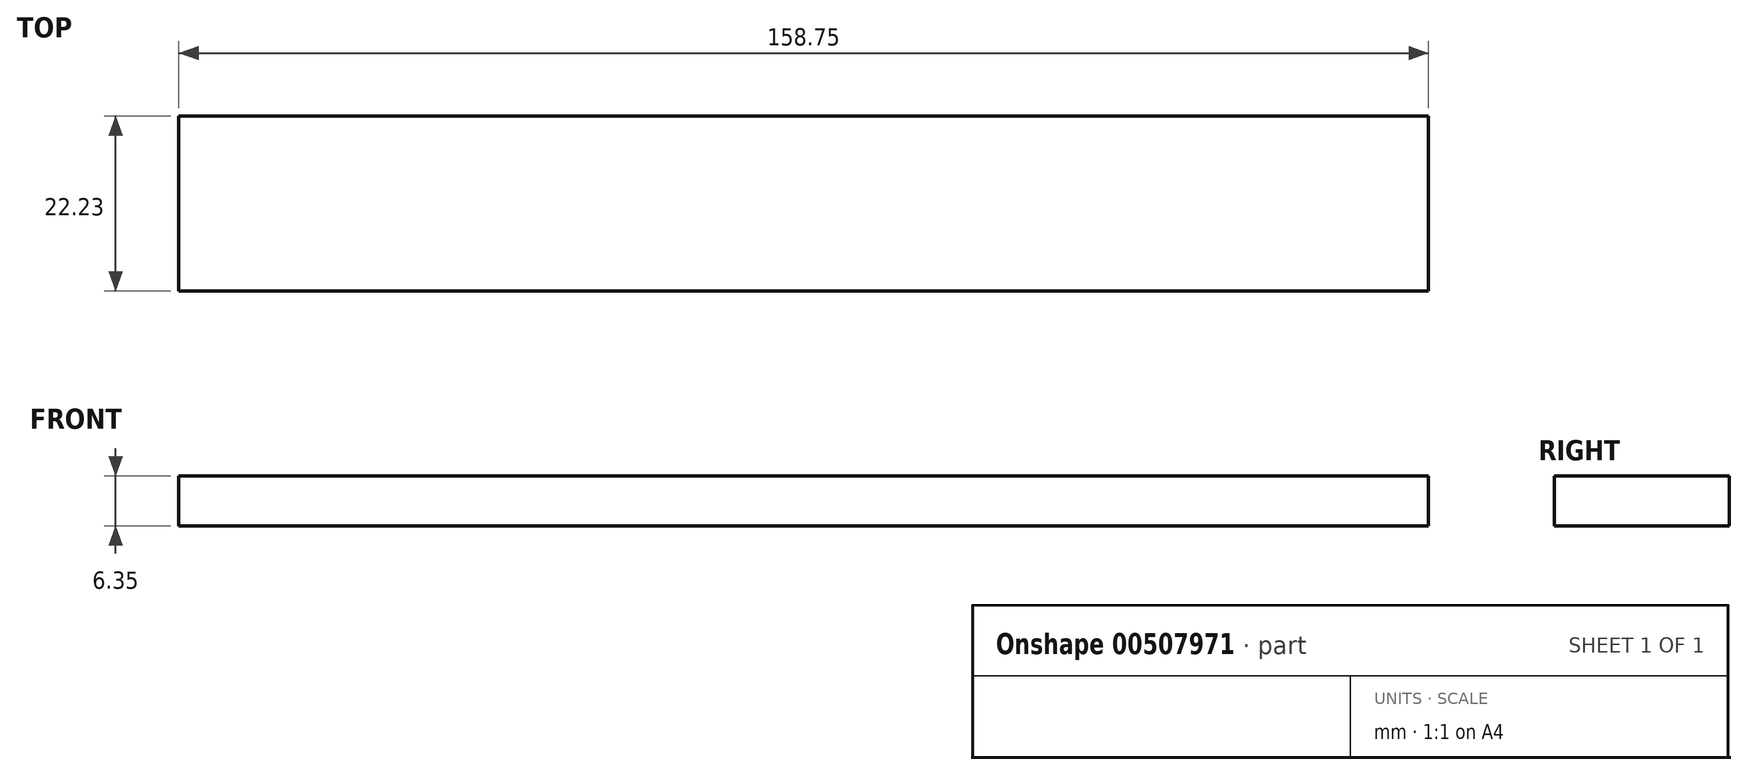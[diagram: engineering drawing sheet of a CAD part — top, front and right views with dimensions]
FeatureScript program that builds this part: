
annotation { "Feature Type Name" : "Feature", "Feature Type Description" : "" }
export const myFeature = defineFeature(function(context is Context, id is Id, definition is map)
    precondition{}
    {
        {
            var Q0;
            Q0=qCreatedBy(makeId("Top.planeOp"),FACE);
            var sketch = newSketch(context, id + "F0", { "sketchPlane" : qUnion([Q0])});
            skLineSegment(sketch, "E0.bottom", {"start": v(0, 0) * mm, "end": v(158.75, 0) * mm});
            skLineSegment(sketch, "E0.top", {"start": v(0, -22.23) * mm, "end": v(158.75, -22.23) * mm});
            skLineSegment(sketch, "E0.left", {"start": v(0, 0) * mm, "end": v(0, -22.23) * mm});
            skLineSegment(sketch, "E0.right", {"start": v(158.75, 0) * mm, "end": v(158.75, -22.22) * mm});
            skSolve(sketch);
        }
        {
            var Q0;
            Q0=makeQuery(id+"F0.imprint","IMPRINT",FACE,{"disambiguationData":[TD([[makeQuery(id+"F0.imprint","IMPRINT",EDGE,{"derivedFrom":sQuery(id+"F0.wireOp",EDGE,"E0.bottom")}),-1.0]])]});
            extrude(context, id + "F1", {"entities" : qUnion([Q0]), "depth" : 6.35 * mm, "offsetDistance" : 25.4 * mm});
        }
    });
